# Revit family: Bidet_Two-Handle-American_Standard-Serin-2064.401
name_source: partatom
category: Plumbing Fixtures
revit_build: Autodesk Revit 2014 (Build: 20130308_1515(x64)
units: mm (PartAtom-declared; Revit-internal decimal feet)

## types (1)
- 2064.401
    ADA Compliant = Yes
    Assembly Code = D2020300
    CW Connection = Yes
    CWFU = 1.5
    Cold Water Connection Diameter = 0' - 0 1/2"
    Cost = 0 $
    Description = Serin Fixture-Mounted Bidet Fitting.
    HW Connection = Yes
    HWFU = 1.5
    Height = 0' - 2 3/4"
    Hot Water Connection Diameter = 0' - 0 1/2"
    Length = 0' - 8"
    Manufacturer = American Standard
    Material = Metal-American Standard-002-Polished Chrome
    Model = 2064.401
    Product Documentation Link = http://www.americanstandard-us.com
    Product URL = http://www.americanstandard-us.com
    Specification = Fixture-Mounted Bidet Fitting. Vacuum breaker. Metal Speed Connect pop-up drain. Lever handles.
    URL = http://www.americanstandard-us.com
    Vent Connection = No
    WFU = 2
    Waste Connection = No
    Width = 0' - 2 1/4"
